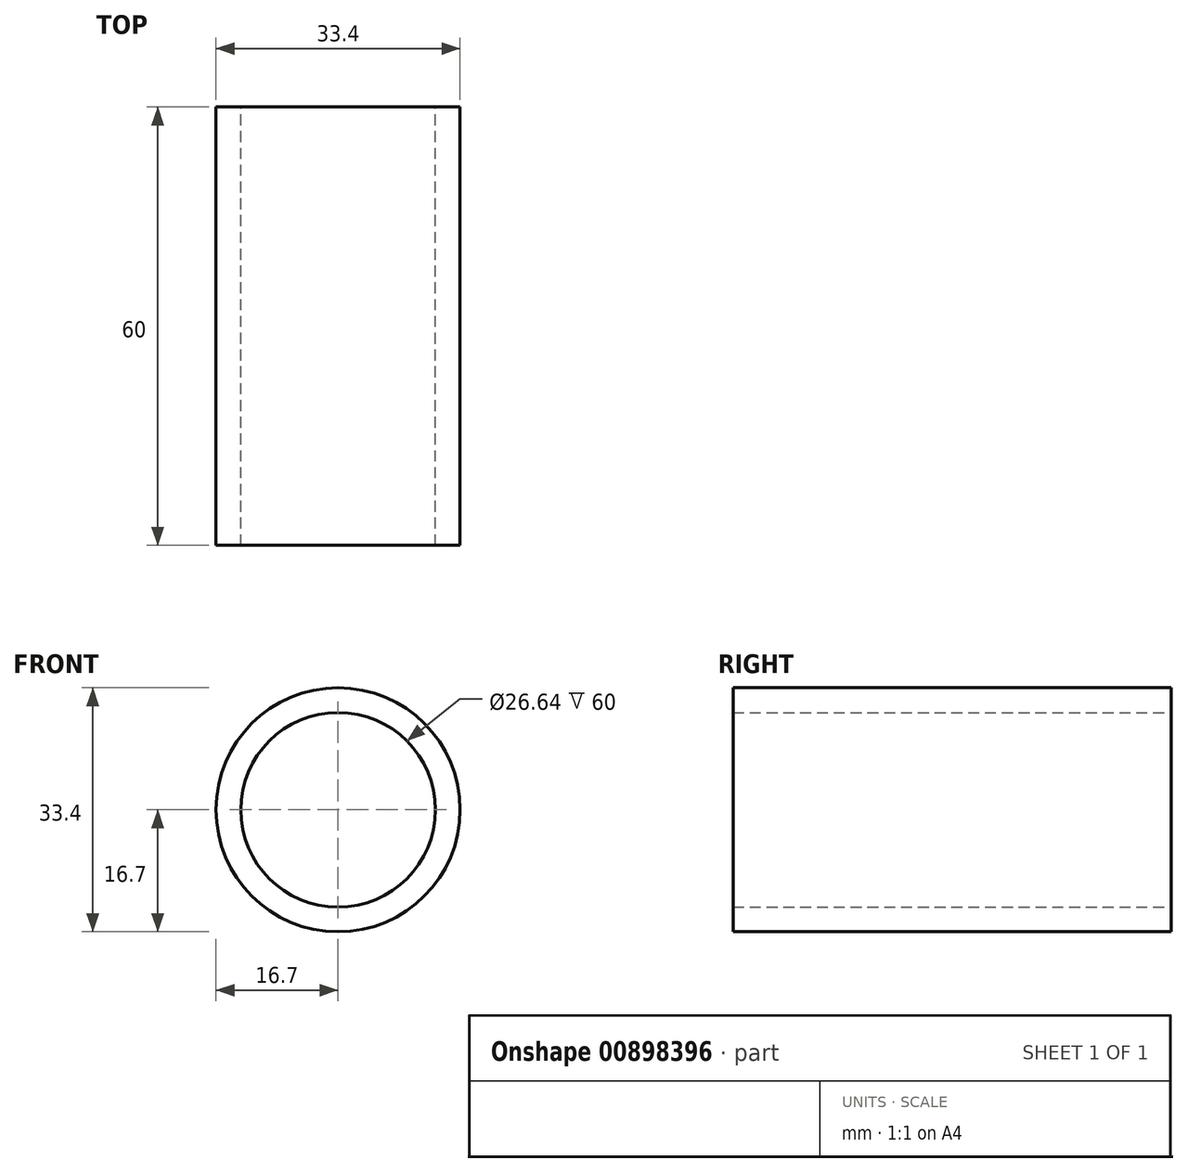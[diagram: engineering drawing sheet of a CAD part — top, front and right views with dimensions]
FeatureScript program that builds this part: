
annotation { "Feature Type Name" : "Feature", "Feature Type Description" : "" }
export const myFeature = defineFeature(function(context is Context, id is Id, definition is map)
    precondition{}
    {
        {
            var Q0;
            Q0=qCreatedBy(makeId("Front.planeOp"),FACE);
            var sketch = newSketch(context, id + "F0", { "sketchPlane" : qUnion([Q0])});
            skCircle(sketch, "E0", {"center": v(0, 0) * mm, "radius": 16.7 * mm});
            skCircle(sketch, "E1", {"center": v(0, 0) * mm, "radius": 13.32 * mm});
            skSolve(sketch);
        }
        {
            var Q0;
            Q0=makeQuery(id+"F0.imprint","IMPRINT",FACE,{"disambiguationData":[TD([[makeQuery(id+"F0.imprint","IMPRINT",EDGE,{"derivedFrom":sQuery(id+"F0.wireOp",EDGE,"E0")}),1.0]])]});
            extrude(context, id + "F1", {"entities" : qUnion([Q0]), "depth" : 60 * mm, "offsetDistance" : 25.4 * mm});
        }
    });
